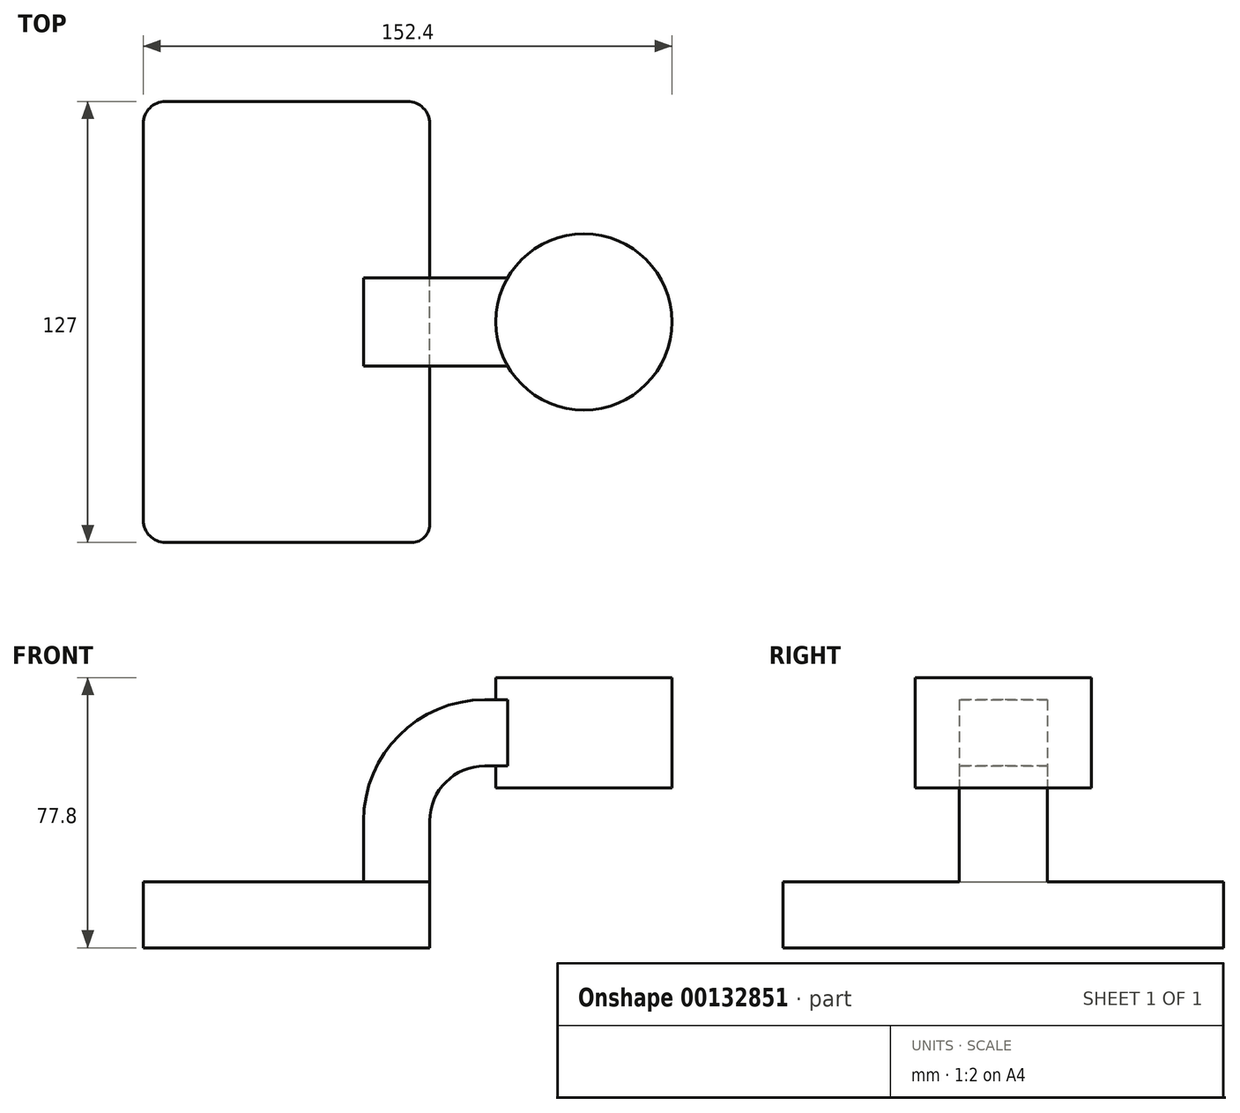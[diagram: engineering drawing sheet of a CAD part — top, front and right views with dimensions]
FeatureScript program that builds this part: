
annotation { "Feature Type Name" : "Feature", "Feature Type Description" : "" }
export const myFeature = defineFeature(function(context is Context, id is Id, definition is map)
    precondition{}
    {
        {
            var Q0;
            Q0=qCreatedBy(makeId("Front.planeOp"),FACE);
            var sketch = newSketch(context, id + "F0", { "sketchPlane" : qUnion([Q0])});
            skLineSegment(sketch, "E0.bottom", {"start": v(-39.36, 11.94) * mm, "end": v(43.2, 11.94) * mm});
            skLineSegment(sketch, "E0.top", {"start": v(-39.36, -7.11) * mm, "end": v(43.2, -7.11) * mm});
            skLineSegment(sketch, "E0.left", {"start": v(-39.36, 11.94) * mm, "end": v(-39.36, -7.11) * mm});
            skLineSegment(sketch, "E0.right", {"start": v(43.2, 11.94) * mm, "end": v(43.2, -7.11) * mm});
            skLineSegment(sketch, "E1", {"start": v(43.2, 11.94) * mm, "end": v(43.2, 29.41) * mm});
            skArc(sketch, "E2", {"start": v(43.2, 29.41) * mm, "mid": v(47.84, 40.64) * mm, "end": v(59.07, 45.29) * mm});
            skLineSegment(sketch, "E3", {"start": v(59.07, 45.29) * mm, "end": v(87.64, 45.29) * mm});
            skLineSegment(sketch, "E4.0", {"start": v(59.07, 64.34) * mm, "end": v(87.64, 64.34) * mm});
            skArc(sketch, "E4.1", {"start": v(24.14, 29.41) * mm, "mid": v(34.37, 54.1) * mm, "end": v(59.07, 64.34) * mm});
            skLineSegment(sketch, "E4.2", {"start": v(24.14, 11.94) * mm, "end": v(24.14, 29.41) * mm});
            skFitSpline(sketch, "E5", {"points": [v(-39.36, 11.94) * mm, v(59.07, 64.34) * mm], "startDerivative": vector(-1.51, 89.25) * mm, "endDerivative": vector(141.83, -1.1) * mm});
            skLineSegment(sketch, "E6", {"start": v(87.64, 70.69) * mm, "end": v(113.04, 70.69) * mm});
            skLineSegment(sketch, "E7", {"start": v(113.04, 70.69) * mm, "end": v(113.04, 38.94) * mm});
            skLineSegment(sketch, "E8", {"start": v(113.04, 38.94) * mm, "end": v(87.64, 38.94) * mm});
            skLineSegment(sketch, "E9", {"start": v(87.64, 38.94) * mm, "end": v(62.24, 38.94) * mm});
            skLineSegment(sketch, "E10", {"start": v(62.24, 38.94) * mm, "end": v(62.24, 70.69) * mm});
            skLineSegment(sketch, "E11", {"start": v(62.24, 70.69) * mm, "end": v(87.64, 70.69) * mm});
            skLineSegment(sketch, "E12", {"start": v(87.64, 38.94) * mm, "end": v(87.64, 70.69) * mm});
            skSolve(sketch);
        }
        {
            var Q0;
            Q0=makeQuery(id+"F0.imprint","IMPRINT",FACE,{"disambiguationData":[TD([[makeQuery(id+"F0.imprint","IMPRINT",EDGE,{"derivedFrom":sQuery(id+"F0.wireOp",EDGE,"E0.top")}),1.0]])]});
            extrude(context, id + "F1", {"entities" : qUnion([Q0]), "endBound" : BoundingType.SYMMETRIC, "depth" : 127 * mm});
        }
        {
            var Q0;
            {var subQ7=sQuery(id+"F0.wireOp",EDGE,"E1");Q0=makeQuery(id+"F0.imprint","IMPRINT",FACE,{"disambiguationData":[TD([[makeQuery(id+"F0.imprint","IMPRINT",EDGE,{"derivedFrom":subQ7}),1.0]])]});}
            var Q1;
            {var subQ0=sQuery(id+"F0.wireOp",EDGE,"MNG41oxj-4DvP-4vhm-BT0C-hKnOCOJBibac.left");var subQ1=sQuery(id+"F0.wireOp",EDGE,"E3");var subQ2=makeQuery(id+"F0.imprint","INTERSECT",VERTEX,{"derivedFrom":[subQ1,subQ0]});Q1=makeQuery(id+"F0.imprint","IMPRINT",FACE,{"disambiguationData":[TD([[makeQuery(id+"F0.imprint","IMPRINT",EDGE,{"disambiguationData":[TD([[subQ2,-1.0]])],"derivedFrom":subQ1}),1.0]])]});}
            extrude(context, id + "F2", {"entities" : qUnion([Q0, Q1]), "operationType" : NewBodyOperationType.ADD, "endBound" : BoundingType.SYMMETRIC, "depth" : 25.4 * mm});
        }
        {
            var Q0;
            Q0=makeQuery(id+"F0.imprint","IMPRINT",FACE,{"disambiguationData":[TD([[makeQuery(id+"F0.imprint","IMPRINT",EDGE,{"derivedFrom":sQuery(id+"F0.wireOp",EDGE,"E4.1")}),1.0]])]});
            extrude(context, id + "F3", {"entities" : qUnion([Q0]), "operationType" : NewBodyOperationType.ADD, "endBound" : BoundingType.SYMMETRIC, "depth" : 15.88 * mm});
        }
        {
            var Q0;
            {var subQ4=sQuery(id+"F0.wireOp",EDGE,"E6");Q0=makeQuery(id+"F0.imprint","IMPRINT",FACE,{"disambiguationData":[TD([[makeQuery(id+"F0.imprint","IMPRINT",EDGE,{"derivedFrom":subQ4}),-1.0]])]});}
            var Q1;
            Q1=sQuery(id+"F0.wireOp",EDGE,"E12");
            revolve(context, id + "F4", {"operationType" : NewBodyOperationType.ADD, "entities" : qUnion([Q0]), "axis" : qUnion([Q1]), "revolveType" : RevolveType.FULL});
        }
        {
            var Q0;
            Q0=makeQuery(id+"F1.opExtrude","CAP_EDGE",EDGE,{"disambiguationData":[OSD([sQuery(id+"F0.wireOp",EDGE,"E0.right")])],"isStart":false});
            fillet(context, id + "F5", {"entities" : qUnion([Q0]), "radius" : 5.08 * mm, "tangentPropagation" : true, "allowEdgeOverflow" : false});
        }
        {
            var Q0;
            Q0=makeQuery(id+"F1.opExtrude","CAP_EDGE",EDGE,{"disambiguationData":[OSD([sQuery(id+"F0.wireOp",EDGE,"E0.left")])],"isStart":false});
            var Q1;
            Q1=makeQuery(id+"F1.opExtrude","CAP_EDGE",EDGE,{"disambiguationData":[OSD([sQuery(id+"F0.wireOp",EDGE,"E0.left")])],"isStart":true});
            var Q2;
            Q2=makeQuery(id+"F1.opExtrude","CAP_EDGE",EDGE,{"disambiguationData":[OSD([sQuery(id+"F0.wireOp",EDGE,"E0.right")])],"isStart":true});
            fillet(context, id + "F6", {"entities" : qUnion([Q0, Q1, Q2]), "radius" : 6.35 * mm, "tangentPropagation" : true, "allowEdgeOverflow" : false});
        }
    });
